# Revit family: Lighting_Fixtures_Hill-Rom_iLED7_i770
name_source: partatom
category: Lighting Fixtures
revit_build: Autodesk Revit Architecture 2015 (Build: 20140606_1530(x64)
units: mm (PartAtom-declared; Revit-internal decimal feet)

## types (1)
- iLED™ 7 Surgical Light (i770)
    ALC Plus = standard
    Ambient Temperature = 10°C to +40°C
    Amperage = 20 A
    Apparent Load = 0 VA
    Average service life of the LEDs = 60000
    BIMobject category = Ceiling Mounted
    BIMobject category code = lighting-ceiling-mounted
    BIMobject main category = Lighting
    BIMobject main category code = lighting
    Brand url = https://construction.hill-rom.com
    Color Filter = 16777215
    Color Rendering Index (Ra) = max 97
    Color Temperature = 3500 K
    Default Elevation = 4' - 0"
    Description = With the latest 3D sensor technology, light field size and intensity of the iLED™ 7 Surgical Light remain consistent regardless of the distance between the light and the surgical site or the position of staff under the lights.
    Design country = United States
    Dimming Lamp Color Temperature Shift = <None>
    Display Material = Glass-Hill Rom-Display
    Edition number = 1
    Frame Material = Plastic-Hill Rom-White
    Frequency = 50 Hz
    Frequency Range = 50-60 Hz
    Full Load Current = 20 A
    Illumination level Ec at 1m = 160000 lx
    Installation instructions = https://construction.hill-rom.com
    Light Source Symbol Size = 2' - 0"
    Manufacturer = Hill-Rom
    Manufacturer country = United States
    Manufacturer name = Hill-Rom
    Masterformat 2014 Code = 26 55 70
    Masterformat 2014 Description = Healthcare Lighting
    Material_display = Glass-Hill Rom-Display
    Material_handles = Plastic-Hill Rom-Blue
    Material_main = Plastic-Hill Rom-White
    Model = iLED™ 7 Surgical Light (i770)
    Nominal height = 0' - 0"
    Nominal width = 0' - 0"
    OmniClass Code = 23-35 47 11 21
    OmniClass Description = Specialized Lighting Fixtures
    Pattern size (d10) at 1m (cm) | (inch) = 16–30 | 6.3”–11.8”
    Power Connector Description = Power Connector Description
    Power Factor = 1
    Product Guid = e68ab167-63d1-4aba-83ab-800f3399a14d
    Product SKU = Trumpf-iLED7-i770
    Product certification = https://www.trumpfmedical.com
    Product data url = https://bimobject.com
    Product family = Surgical Lights
    Product group = iLed7
    Product url = https://www.trumpfmedical.com
    QR code = http://bimobject.com
    Relative humidity = 30% to 75%
    SLC = Optional
    Technical description = https://construction.hill-rom.com
    UNSPSC Code = 39101602
    URL = https://www.hill-rom.com
    Uniclass 1.4 Code = L747331
    Uniclass 1.4 Description = Medical/hospital lighting
    Voltage = 120 V
    Voltage Range = 100-240V
    Weight Net (Kg) = 0
    Youtube clip = https://www.youtube.com

## geometry (parser evidence)
native form markers: Blend x2, Sweep x4
no freeform markers — native parametric forms only
